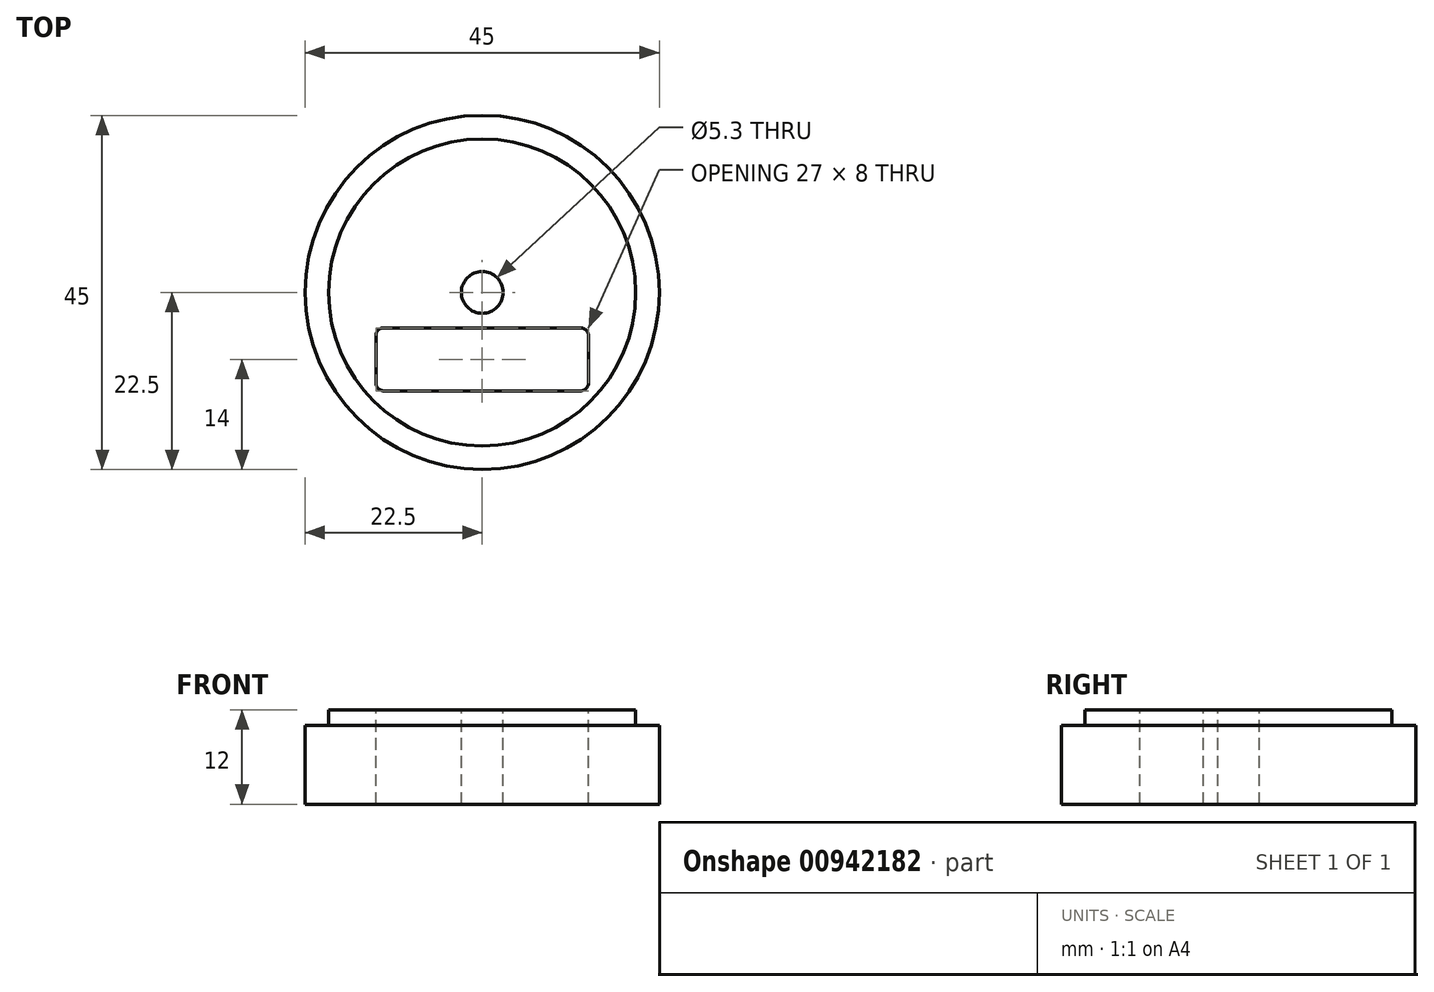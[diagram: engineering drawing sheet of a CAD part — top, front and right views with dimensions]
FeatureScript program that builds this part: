
annotation { "Feature Type Name" : "Feature", "Feature Type Description" : "" }
export const myFeature = defineFeature(function(context is Context, id is Id, definition is map)
    precondition{}
    {
        {
            var Q0;
            Q0=qCreatedBy(makeId("Top.planeOp"),FACE);
            var sketch = newSketch(context, id + "F0", { "sketchPlane" : qUnion([Q0])});
            skCircle(sketch, "E0", {"center": v(0, 0) * mm, "radius": 22.5 * mm});
            skSolve(sketch);
        }
        {
            var Q0;
            Q0=makeQuery(id+"F0.imprint","IMPRINT",FACE,{"disambiguationData":[TD([[makeQuery(id+"F0.imprint","IMPRINT",EDGE,{"derivedFrom":sQuery(id+"F0.wireOp",EDGE,"E0")}),1.0]])]});
            extrude(context, id + "F1", {"entities" : qUnion([Q0]), "depth" : 10 * mm, "offsetDistance" : 25 * mm});
        }
        {
            var Q0;
            Q0=qCreatedBy(makeId("Top.planeOp"),FACE);
            var sketch = newSketch(context, id + "F2", { "sketchPlane" : qUnion([Q0])});
            skLineSegment(sketch, "E1", {"start": v(22.36, -2.5) * mm, "end": v(-22.36, -2.5) * mm, "construction": true});
            skLineSegment(sketch, "E2", {"start": v(14.5, -4.5) * mm, "end": v(-14.5, -4.5) * mm, "construction": true});
            skLineSegment(sketch, "E3", {"start": v(14, -6.3) * mm, "end": v(-14, -6.3) * mm, "construction": true});
            skLineSegment(sketch, "E4", {"start": v(8, -8.3) * mm, "end": v(-8, -8.3) * mm, "construction": true});
            skLineSegment(sketch, "E5", {"start": v(-8, -8.3) * mm, "end": v(-8, -6.3) * mm, "construction": true});
            skLineSegment(sketch, "E6", {"start": v(8, -8.3) * mm, "end": v(8, -6.3) * mm, "construction": true});
            skPoint(sketch, "E7", {"position": v(0, -8.3) * mm});
            skLineSegment(sketch, "E8", {"start": v(14.5, -4.5) * mm, "end": v(14.5, -2.5) * mm, "construction": true});
            skLineSegment(sketch, "E9", {"start": v(-14.5, -4.5) * mm, "end": v(-14.5, -2.5) * mm, "construction": true});
            skPoint(sketch, "E10", {"position": v(0, -4.5) * mm});
            skPoint(sketch, "E11", {"position": v(0, -6.3) * mm});
            skLineSegment(sketch, "E12", {"start": v(14, -6.3) * mm, "end": v(14, -4.5) * mm, "construction": true});
            skLineSegment(sketch, "E13", {"start": v(-14, -6.3) * mm, "end": v(-14, -4.5) * mm, "construction": true});
            skLineSegment(sketch, "E14.bottom", {"start": v(-14, -9.9) * mm, "end": v(14, -9.9) * mm, "construction": true});
            skLineSegment(sketch, "E14.top", {"start": v(-14, -8.3) * mm, "end": v(14, -8.3) * mm, "construction": true});
            skLineSegment(sketch, "E14.left", {"start": v(-14, -9.9) * mm, "end": v(-14, -8.3) * mm, "construction": true});
            skLineSegment(sketch, "E14.right", {"start": v(14, -9.9) * mm, "end": v(14, -8.3) * mm, "construction": true});
            skPoint(sketch, "E15", {"position": v(0, -9.9) * mm});
            skSolve(sketch);
        }
        {
            var Q0;
            Q0=makeQuery(id+"F1.opExtrude","CAP_FACE",FACE,{"disambiguationData":[OSD([sQuery(id+"F0.wireOp",EDGE,"E0"),sQuery(id+"F0.wireOp",EDGE,"LeQiM02k-lcOv-xtmz-SaLr-1kOP8s4PphW9")])],"isStart":false});
            var sketch = newSketch(context, id + "F3", { "sketchPlane" : qUnion([Q0])});
            skCircle(sketch, "E16", {"center": v(0, 0) * mm, "radius": 19.5 * mm});
            skSolve(sketch);
        }
        {
            var Q0;
            Q0 = qSketchRegion(id + "F3", true);
            extrude(context, id + "F4", {"entities" : qUnion([Q0]), "operationType" : NewBodyOperationType.ADD, "depth" : 2 * mm, "offsetDistance" : 25 * mm});
        }
        {
            var Q0;
            Q0=makeQuery(id+"F4.opExtrude","CAP_FACE",FACE,{"disambiguationData":[OSD([sQuery(id+"F3.wireOp",EDGE,"E16")])],"isStart":false});
            var sketch = newSketch(context, id + "F5", { "sketchPlane" : qUnion([Q0])});
            skCircle(sketch, "E17", {"center": v(0, 0) * mm, "radius": 2.65 * mm});
            skLineSegment(sketch, "E18.bottom", {"start": v(13.5, -4.5) * mm, "end": v(-13.5, -4.5) * mm});
            skLineSegment(sketch, "E18.top", {"start": v(13.5, -12.5) * mm, "end": v(-13.5, -12.5) * mm});
            skLineSegment(sketch, "E18.left", {"start": v(13.5, -4.5) * mm, "end": v(13.5, -12.5) * mm});
            skLineSegment(sketch, "E18.right", {"start": v(-13.5, -4.5) * mm, "end": v(-13.5, -12.5) * mm});
            skPoint(sketch, "E19", {"position": v(0, -4.5) * mm});
            skSolve(sketch);
        }
        {
            var Q0;
            Q0 = qSketchRegion(id + "F5", true);
            extrude(context, id + "F6", {"entities" : qUnion([Q0]), "operationType" : NewBodyOperationType.REMOVE, "endBound" : BoundingType.THROUGH_ALL, "oppositeDirection" : true, "depth" : 25 * mm, "offsetDistance" : 25 * mm});
        }
        {
            var Q0;
            Q0=makeQuery(id+"F1.opExtrude","CAP_FACE",FACE,{"disambiguationData":[OSD([sQuery(id+"F0.wireOp",EDGE,"E0")])],"isStart":true});
            var sketch = newSketch(context, id + "F7", { "sketchPlane" : qUnion([Q0])});
            skCircle(sketch, "E20", {"center": v(0, 0) * mm, "radius": 6 * mm});
            skSolve(sketch);
        }
        {
            var Q0;
            Q0=makeQuery(id+"F7587SFKQXNkNbu_1.boolean.opBoolean","INTERSECT",EDGE,{"disambiguationData":[OD(0.0)],"derivedFrom":[makeQuery(id+"F6.boolean.opBoolean","COPY",FACE,{"derivedFrom":makeQuery(id+"F6.opExtrude","SWEPT_FACE",FACE,{"disambiguationData":[OSD([sQuery(id+"F5.wireOp",EDGE,"E18.bottom")])]})}),makeQuery(id+"F7587SFKQXNkNbu_1.opExtrude","SWEPT_FACE",FACE,{"disambiguationData":[OSD([sQuery(id+"F7.wireOp",EDGE,"E20")])]})]});
            var Q1;
            Q1=makeQuery(id+"F7587SFKQXNkNbu_1.boolean.opBoolean","INTERSECT",EDGE,{"disambiguationData":[OD(1.0)],"derivedFrom":[makeQuery(id+"F6.boolean.opBoolean","COPY",FACE,{"derivedFrom":makeQuery(id+"F6.opExtrude","SWEPT_FACE",FACE,{"disambiguationData":[OSD([sQuery(id+"F5.wireOp",EDGE,"E18.bottom")])]})}),makeQuery(id+"F7587SFKQXNkNbu_1.opExtrude","SWEPT_FACE",FACE,{"disambiguationData":[OSD([sQuery(id+"F7.wireOp",EDGE,"E20")])]})]});
            var Q2;
            Q2=makeQuery(id+"F6.boolean.opBoolean","COPY",EDGE,{"derivedFrom":makeQuery(id+"F6.opExtrude","SWEPT_EDGE",EDGE,{"disambiguationData":[OSD([sQuery(id+"F5.wireOp",EDGE,"E18.top"),sQuery(id+"F5.wireOp",EDGE,"E18.right")])]})});
            var Q3;
            Q3=makeQuery(id+"F6.boolean.opBoolean","COPY",EDGE,{"derivedFrom":makeQuery(id+"F6.opExtrude","SWEPT_EDGE",EDGE,{"disambiguationData":[OSD([sQuery(id+"F5.wireOp",EDGE,"E18.bottom"),sQuery(id+"F5.wireOp",EDGE,"E18.right")])]})});
            var Q4;
            Q4=makeQuery(id+"F6.boolean.opBoolean","COPY",EDGE,{"derivedFrom":makeQuery(id+"F6.opExtrude","SWEPT_EDGE",EDGE,{"disambiguationData":[OSD([sQuery(id+"F5.wireOp",EDGE,"E18.bottom"),sQuery(id+"F5.wireOp",EDGE,"E18.left")])]})});
            var Q5;
            Q5=makeQuery(id+"F6.boolean.opBoolean","COPY",EDGE,{"derivedFrom":makeQuery(id+"F6.opExtrude","SWEPT_EDGE",EDGE,{"disambiguationData":[OSD([sQuery(id+"F5.wireOp",EDGE,"E18.top"),sQuery(id+"F5.wireOp",EDGE,"E18.left")])]})});
            fillet(context, id + "F8", {"entities" : qUnion([Q0, Q1, Q2, Q3, Q4, Q5]), "radius" : 1 * mm, "tangentPropagation" : true, "allowEdgeOverflow" : false});
        }
    });
